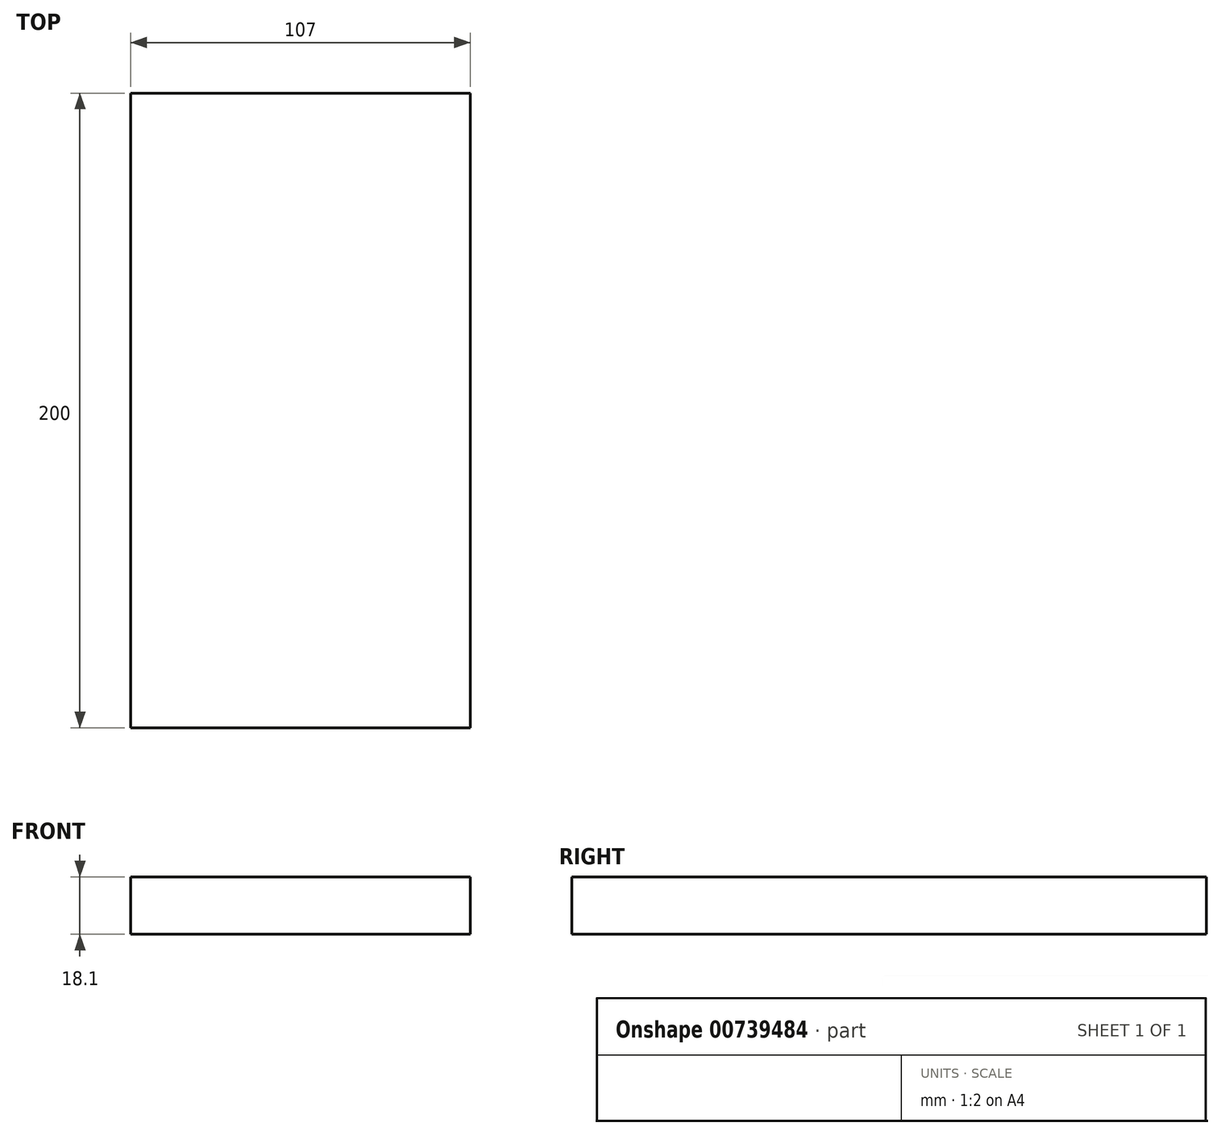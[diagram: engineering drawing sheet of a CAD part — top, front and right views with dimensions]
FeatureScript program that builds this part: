
annotation { "Feature Type Name" : "Feature", "Feature Type Description" : "" }
export const myFeature = defineFeature(function(context is Context, id is Id, definition is map)
    precondition{}
    {
        {
            var Q0;
            Q0=qCreatedBy(makeId("Top.planeOp"),FACE);
            var sketch = newSketch(context, id + "F0", { "sketchPlane" : qUnion([Q0])});
            skLineSegment(sketch, "E0.bottom", {"start": v(-53.5, 100) * mm, "end": v(53.5, 100) * mm});
            skLineSegment(sketch, "E0.top", {"start": v(-53.5, -100) * mm, "end": v(53.5, -100) * mm});
            skLineSegment(sketch, "E0.left", {"start": v(-53.5, 100) * mm, "end": v(-53.5, -100) * mm});
            skLineSegment(sketch, "E0.right", {"start": v(53.5, 100) * mm, "end": v(53.5, -100) * mm});
            skPoint(sketch, "E0.middle", {"position": v(0, 0) * mm});
            skSolve(sketch);
        }
        {
            var Q0;
            Q0=makeQuery(id+"F0.imprint","IMPRINT",FACE,{"disambiguationData":[TD([[makeQuery(id+"F0.imprint","IMPRINT",EDGE,{"derivedFrom":sQuery(id+"F0.wireOp",EDGE,"E0.bottom")}),-1.0]])]});
            extrude(context, id + "F1", {"entities" : qUnion([Q0]), "depth" : 18.1 * mm, "offsetDistance" : 25 * mm});
        }
    });
